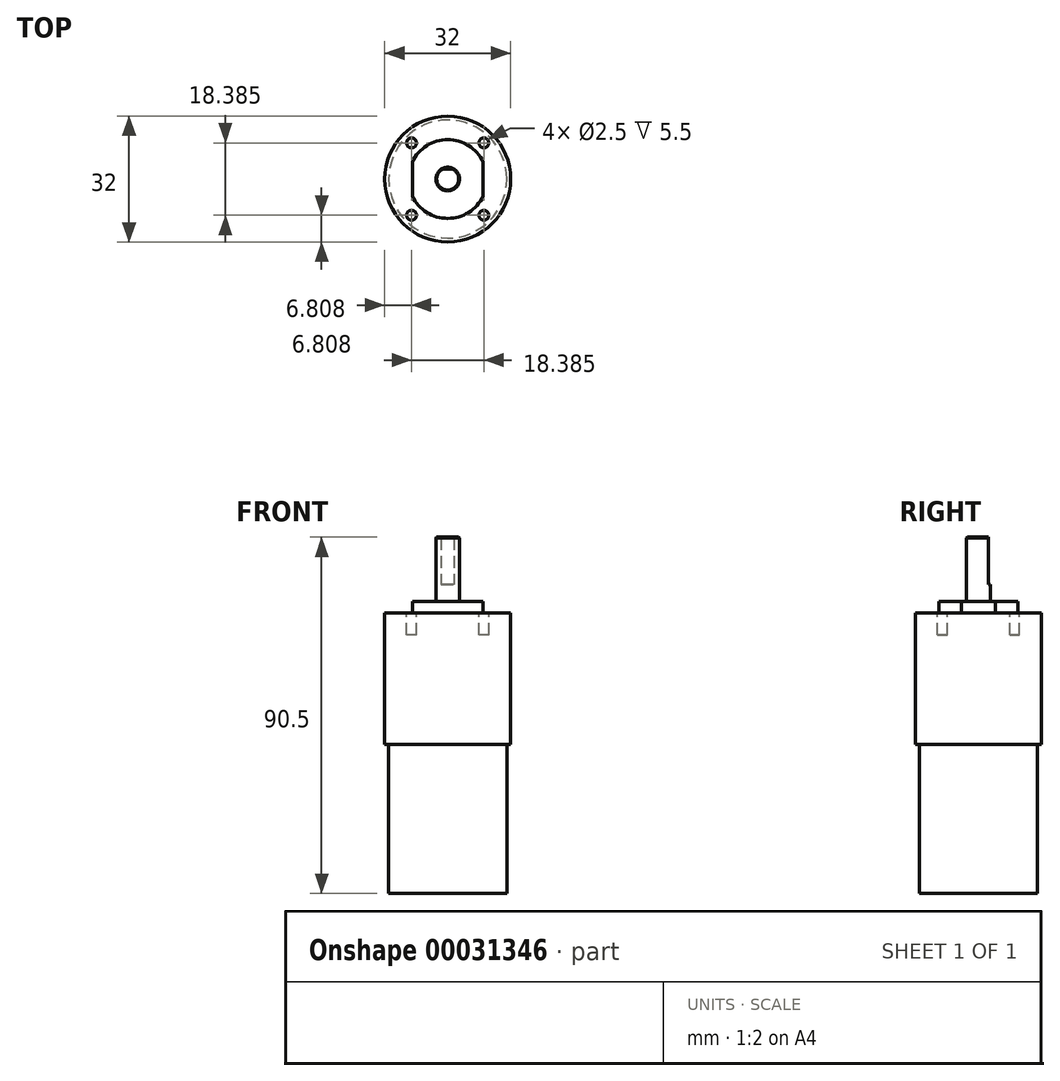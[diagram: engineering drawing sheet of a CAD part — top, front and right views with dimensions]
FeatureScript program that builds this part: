
annotation { "Feature Type Name" : "Feature", "Feature Type Description" : "" }
export const myFeature = defineFeature(function(context is Context, id is Id, definition is map)
    precondition{}
    {
        {
            var Q0;
            Q0=qCreatedBy(makeId("Top.planeOp"),FACE);
            var sketch = newSketch(context, id + "F0", { "sketchPlane" : qUnion([Q0])});
            skCircle(sketch, "E0", {"center": v(0, 0) * mm, "radius": 15 * mm});
            skSolve(sketch);
        }
        {
            var Q0;
            Q0=makeQuery(id+"F0.imprint","IMPRINT",FACE,{"disambiguationData":[TD([[makeQuery(id+"F0.imprint","IMPRINT",EDGE,{"derivedFrom":sQuery(id+"F0.wireOp",EDGE,"E0")}),1.0]])]});
            extrude(context, id + "F1", {"entities" : qUnion([Q0]), "depth" : 37.8 * mm});
        }
        {
            var Q0;
            Q0=makeQuery(id+"F1.opExtrude","CAP_FACE",FACE,{"disambiguationData":[OSD([sQuery(id+"F0.wireOp",EDGE,"E0")])],"isStart":false});
            var sketch = newSketch(context, id + "F2", { "sketchPlane" : qUnion([Q0])});
            skCircle(sketch, "E1", {"center": v(0, 0) * mm, "radius": 16 * mm});
            skSolve(sketch);
        }
        {
            var Q0;
            Q0 = qSketchRegion(id + "F2", true);
            extrude(context, id + "F3", {"entities" : qUnion([Q0]), "operationType" : NewBodyOperationType.ADD, "depth" : 33.4 * mm});
        }
        {
            var Q0;
            Q0=makeQuery(id+"F3.opExtrude","CAP_FACE",FACE,{"disambiguationData":[OSD([sQuery(id+"F2.wireOp",EDGE,"E1")])],"isStart":false});
            var sketch = newSketch(context, id + "F4", { "sketchPlane" : qUnion([Q0])});
            skArc(sketch, "E2", {"start": v(-9, -4.36) * mm, "mid": v(0, -10) * mm, "end": v(9, -4.36) * mm});
            skLineSegment(sketch, "E3", {"start": v(-9, 4.36) * mm, "end": v(-9, -4.36) * mm});
            skLineSegment(sketch, "E4", {"start": v(9, 4.36) * mm, "end": v(9, -4.36) * mm});
            skArc(sketch, "E5.trimOffspring", {"start": v(9, 4.36) * mm, "mid": v(0, 10) * mm, "end": v(-9, 4.36) * mm});
            skSolve(sketch);
        }
        {
            var Q0;
            Q0 = qSketchRegion(id + "F4", true);
            extrude(context, id + "F5", {"entities" : qUnion([Q0]), "operationType" : NewBodyOperationType.ADD, "depth" : 3 * mm});
        }
        {
            var Q0;
            Q0=makeQuery(id+"F5.opExtrude","CAP_FACE",FACE,{"disambiguationData":[OSD([sQuery(id+"F4.wireOp",EDGE,"E2"),sQuery(id+"F4.wireOp",EDGE,"E3"),sQuery(id+"F4.wireOp",EDGE,"E4"),sQuery(id+"F4.wireOp",EDGE,"E5.trimOffspring")])],"isStart":false});
            var sketch = newSketch(context, id + "F6", { "sketchPlane" : qUnion([Q0])});
            skLineSegment(sketch, "E6", {"start": v(1.31, 1.98) * mm, "end": v(1.31, 1.98) * mm});
            skCircle(sketch, "E7", {"center": v(0, 0) * mm, "radius": 3 * mm});
            skSolve(sketch);
        }
        {
            var Q0;
            Q0 = qSketchRegion(id + "F6", true);
            extrude(context, id + "F7", {"entities" : qUnion([Q0]), "operationType" : NewBodyOperationType.ADD, "depth" : 4.3 * mm});
        }
        {
            var Q0;
            Q0=makeQuery(id+"F7.opExtrude","CAP_FACE",FACE,{"disambiguationData":[OSD([sQuery(id+"F6.wireOp",EDGE,"E7")])],"isStart":false});
            var sketch = newSketch(context, id + "F8", { "sketchPlane" : qUnion([Q0])});
            skArc(sketch, "E8", {"start": v(-1.66, 2.5) * mm, "mid": v(0, -3) * mm, "end": v(1.66, 2.5) * mm});
            skLineSegment(sketch, "E9", {"start": v(-1.66, 2.5) * mm, "end": v(1.66, 2.5) * mm});
            skSolve(sketch);
        }
        {
            var Q0;
            Q0 = qSketchRegion(id + "F8", true);
            extrude(context, id + "F9", {"entities" : qUnion([Q0]), "operationType" : NewBodyOperationType.ADD, "depth" : 12 * mm});
        }
        {
            var Q0;
            Q0=makeQuery(id+"F9.opExtrude","CAP_EDGE",EDGE,{"disambiguationData":[OSD([sQuery(id+"F8.wireOp",EDGE,"E8")])],"isStart":false});
            chamfer(context, id + "F10", {"entities" : qUnion([Q0]), "width" : 0.2 * mm, "tangentPropagation" : true});
        }
        {
            var Q0;
            Q0=makeQuery(id+"F3.opExtrude","CAP_FACE",FACE,{"disambiguationData":[OSD([sQuery(id+"F2.wireOp",EDGE,"E1")])],"isStart":false});
            var sketch = newSketch(context, id + "F11", { "sketchPlane" : qUnion([Q0])});
            skCircle(sketch, "E10", {"center": v(9.2, -9.2) * mm, "radius": 1.25 * mm});
            skCircle(sketch, "E11", {"center": v(-9.2, -9.2) * mm, "radius": 1.25 * mm});
            skCircle(sketch, "E12", {"center": v(9.2, 9.2) * mm, "radius": 1.25 * mm});
            skCircle(sketch, "E13", {"center": v(-9.2, 9.2) * mm, "radius": 1.25 * mm});
            skLineSegment(sketch, "E14", {"start": v(0, 0) * mm, "end": v(13.48, 13.48) * mm, "construction": true});
            skLineSegment(sketch, "E15", {"start": v(0, 0) * mm, "end": v(-14.04, 14.04) * mm, "construction": true});
            skLineSegment(sketch, "E16", {"start": v(0, 0) * mm, "end": v(-12.84, -12.84) * mm, "construction": true});
            skLineSegment(sketch, "E17", {"start": v(0, 0) * mm, "end": v(14.58, -14.58) * mm, "construction": true});
            skCircle(sketch, "E18", {"center": v(0, 0) * mm, "radius": 13 * mm, "construction": true});
            skLineSegment(sketch, "E19", {"start": v(-15.7, -9.2) * mm, "end": v(19.7, -9.2) * mm, "construction": true});
            skSolve(sketch);
        }
        {
            var Q0;
            Q0 = qSketchRegion(id + "F11", true);
            var Q1;
            Q1 = qConstructionFilter(qBodyType(qCreatedBy(id + "F11" ,EDGE), BodyType.WIRE), ConstructionObject.NO);
            extrude(context, id + "F12", {"entities" : qUnion([Q0]), "operationType" : NewBodyOperationType.REMOVE, "surfaceEntities" : qUnion([Q1]), "oppositeDirection" : true, "depth" : 5.5 * mm});
        }
    });
